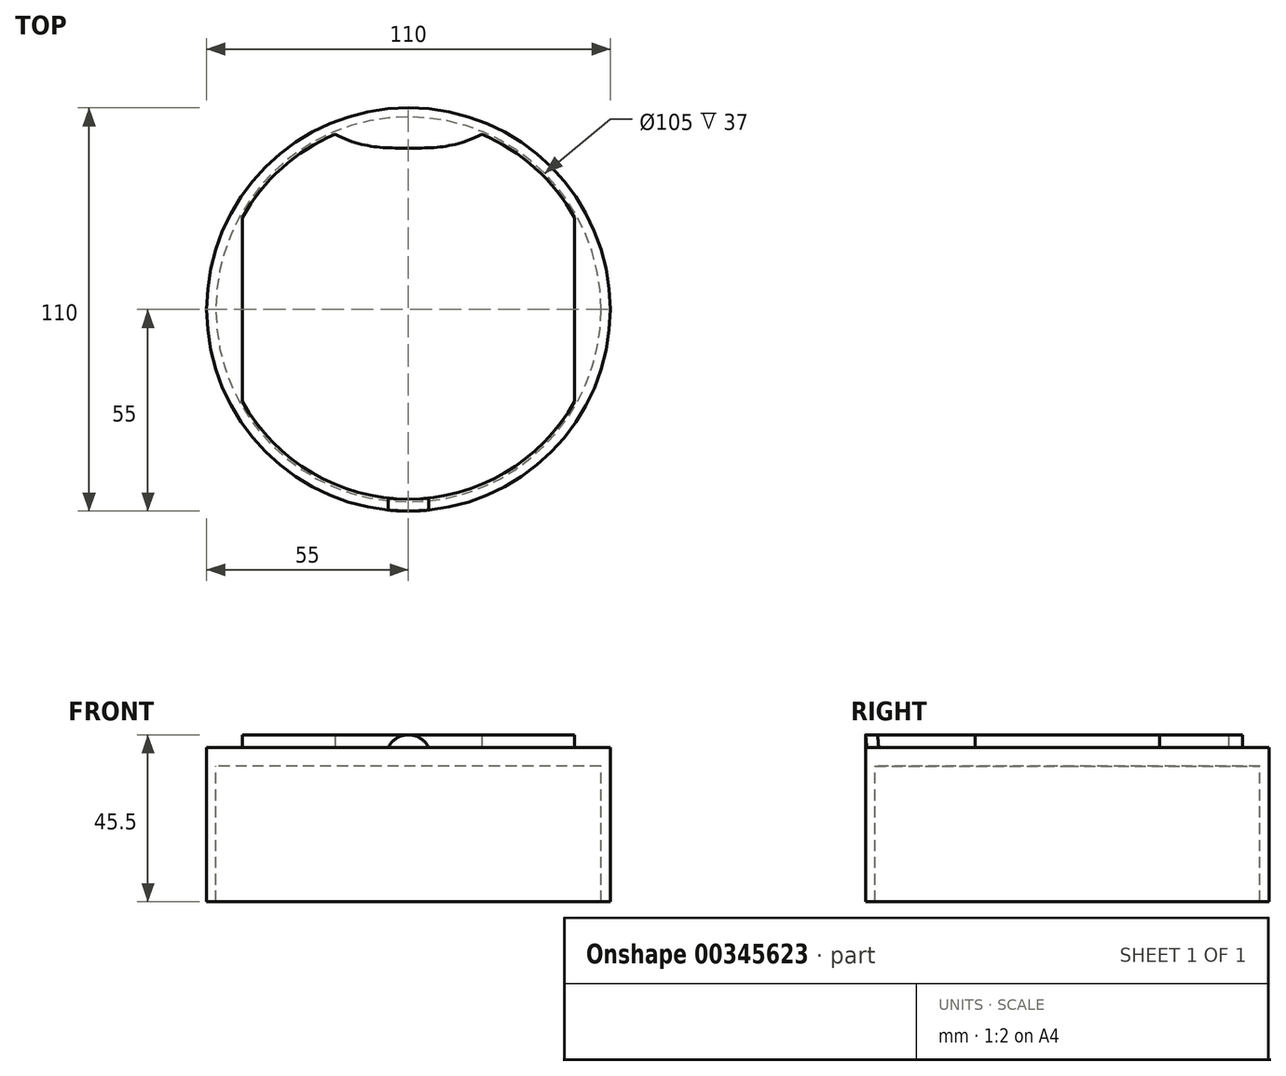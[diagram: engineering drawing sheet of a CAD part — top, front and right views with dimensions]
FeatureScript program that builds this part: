
annotation { "Feature Type Name" : "Feature", "Feature Type Description" : "" }
export const myFeature = defineFeature(function(context is Context, id is Id, definition is map)
    precondition{}
    {
        {
            var Q0;
            Q0=qCreatedBy(makeId("Top.planeOp"),FACE);
            var sketch = newSketch(context, id + "F0", { "sketchPlane" : qUnion([Q0])});
            skCircle(sketch, "E0", {"center": v(0, 0) * mm, "radius": 55 * mm});
            skCircle(sketch, "E1", {"center": v(0, 0) * mm, "radius": 52.5 * mm});
            skArc(sketch, "E2", {"start": v(45.25, 25.1) * mm, "mid": v(34.53, 38.55) * mm, "end": v(20, 47.73) * mm});
            skLineSegment(sketch, "E3", {"start": v(-45.25, 25.1) * mm, "end": v(-45.25, -25.1) * mm});
            skLineSegment(sketch, "E4", {"start": v(45.25, 25.1) * mm, "end": v(45.25, -25.1) * mm});
            skArc(sketch, "E5.trimOffspring", {"start": v(-45.25, -25.1) * mm, "mid": v(0, -51.75) * mm, "end": v(45.25, -25.1) * mm});
            skPoint(sketch, "E6.middle", {"position": v(0, 44) * mm});
            skFitSpline(sketch, "E7", {"points": [v(0, 44) * mm, v(20, 47.73) * mm], "startDerivative": vector(21.3, 0) * mm, "endDerivative": vector(22.52, 11.19) * mm});
            skPoint(sketch, "E8", {"position": v(20, 44) * mm});
            skFitSpline(sketch, "E9.MirrorCS", {"points": [v(0, 44) * mm, v(-20, 47.73) * mm], "startDerivative": vector(-21.3, 0) * mm, "endDerivative": vector(-22.52, 11.19) * mm});
            skArc(sketch, "E10.trimOffspring", {"start": v(-20, 47.73) * mm, "mid": v(-34.53, 38.55) * mm, "end": v(-45.25, 25.1) * mm});
            skPoint(sketch, "E11.orphan", {"position": v(0, 55) * mm});
            skPoint(sketch, "E12.middle", {"position": v(0, -55) * mm});
            skLineSegment(sketch, "E13.left", {"start": v(5.5, -51.46) * mm, "end": v(5.5, -54.72) * mm});
            skLineSegment(sketch, "E13.right", {"start": v(-5.5, -51.46) * mm, "end": v(-5.5, -54.72) * mm});
            skSolve(sketch);
        }
        {
            var Q0;
            Q0=makeQuery(id+"F0.imprint","IMPRINT",FACE,{"disambiguationData":[TD([[makeQuery(id+"F0.imprint","IMPRINT",EDGE,{"derivedFrom":sQuery(id+"F0.wireOp",EDGE,"E1")}),1.0]])]});
            var Q1;
            Q1=makeQuery(id+"F0.imprint","IMPRINT",FACE,{"disambiguationData":[TD([[makeQuery(id+"F0.imprint","IMPRINT",EDGE,{"derivedFrom":sQuery(id+"F0.wireOp",EDGE,"E0")}),1.0]])]});
            var Q2;
            Q2=makeQuery(id+"F0.imprint","IMPRINT",FACE,{"disambiguationData":[TD([[makeQuery(id+"F0.imprint","IMPRINT",EDGE,{"derivedFrom":sQuery(id+"F0.wireOp",EDGE,"E2")}),-1.0]])]});
            var Q3;
            Q3=makeQuery(id+"F0.imprint","IMPRINT",FACE,{"disambiguationData":[TD([[makeQuery(id+"F0.imprint","IMPRINT",EDGE,{"derivedFrom":sQuery(id+"F0.wireOp",EDGE,"E2")}),1.0]])]});
            extrude(context, id + "F1", {"entities" : qUnion([Q0, Q1, Q2, Q3]), "oppositeDirection" : true, "depth" : 5 * mm});
        }
        {
            var Q0;
            Q0=makeQuery(id+"F0.imprint","IMPRINT",FACE,{"disambiguationData":[TD([[makeQuery(id+"F0.imprint","IMPRINT",EDGE,{"derivedFrom":sQuery(id+"F0.wireOp",EDGE,"E0")}),1.0]])]});
            extrude(context, id + "F2", {"entities" : qUnion([Q0]), "operationType" : NewBodyOperationType.ADD, "oppositeDirection" : true, "depth" : 42 * mm});
        }
        {
            var Q0;
            Q0=makeQuery(id+"F0.imprint","IMPRINT",FACE,{"disambiguationData":[TD([[makeQuery(id+"F0.imprint","IMPRINT",EDGE,{"derivedFrom":sQuery(id+"F0.wireOp",EDGE,"E2")}),1.0]])]});
            extrude(context, id + "F3", {"entities" : qUnion([Q0]), "depth" : 3.5 * mm});
        }
        {
            var Q0;
            {var subQ0=sQuery(id+"F0.wireOp",EDGE,"E13.left");var subQ1=sQuery(id+"F0.wireOp",EDGE,"E0");var subQ2=makeQuery(id+"F0.imprint","INTERSECT",VERTEX,{"derivedFrom":[subQ1,subQ0]});Q0=makeQuery(id+"F0.imprint","IMPRINT",FACE,{"disambiguationData":[TD([[makeQuery(id+"F0.imprint","IMPRINT",EDGE,{"disambiguationData":[TD([[subQ2,1.0]])],"derivedFrom":subQ1}),1.0]])]});}
            var Q1;
            {var subQ0=sQuery(id+"F0.wireOp",EDGE,"E13.left");var subQ1=sQuery(id+"F0.wireOp",EDGE,"E1");var subQ2=makeQuery(id+"F0.imprint","INTERSECT",VERTEX,{"derivedFrom":[subQ1,subQ0]});Q1=makeQuery(id+"F0.imprint","IMPRINT",FACE,{"disambiguationData":[TD([[makeQuery(id+"F0.imprint","IMPRINT",EDGE,{"disambiguationData":[TD([[subQ2,1.0]])],"derivedFrom":subQ1}),1.0]])]});}
            extrude(context, id + "F4", {"entities" : qUnion([Q0, Q1]), "depth" : 3.5 * mm});
        }
        {
            var Q0;
            Q0=makeQuery(id+"F4.opExtrude","CAP_EDGE",EDGE,{"disambiguationData":[OSD([sQuery(id+"F0.wireOp",EDGE,"E13.left")])],"isStart":false});
            var Q1;
            Q1=makeQuery(id+"F4.opExtrude","CAP_EDGE",EDGE,{"disambiguationData":[OSD([sQuery(id+"F0.wireOp",EDGE,"E13.right")])],"isStart":false});
            fillet(context, id + "F5", {"entities" : qUnion([Q0, Q1]), "radius" : 6 * mm, "tangentPropagation" : true, "allowEdgeOverflow" : false});
        }
    });
